# Revit family: DBLTD_TheSenatorGroup_LoungeChairs_Aura_Straight_US
name_source: partatom
category: Furniture
units: mm (PartAtom-declared; Revit-internal decimal feet)

## family parameters
Always vertical = Yes
Cut with Voids When Loaded = No
OmniClass Number = 23.40.20.00
OmniClass Title = General Furniture and Specialties
Render Appearance Source = Family Geometry
Room Calculation Point = No
Shared = Yes
Work Plane-Based = No

## types (26) — shared parameters
Assembly Code = E2020200
AssetType = Movable
Category = Pr_40_50_12_57 Office chairs
Color = Upholstery: Various Options Available
DurationUnit = years
ExpectedLife = 5
Finish = Upholstery: Various Options Available
Keynote = Pr_40_50_12_57 Office chairs
Manufacturer = The Senator Group
ManufacturerName = The Senator Group
ManufacturerURL = https://www.allermuir.com
Material = Cut Foam Seat Carcass | Fully Upholstered | Plastic Glides with Felt
Name = Lounge Sofa
NominalDepth = 38 "
ProductInformation = https://www.allermuir.com
SeatingHeight = 16 "
Shape = Rectangular
URL = https://www.thesenatorgroup.com
Uniclass2015Code = Pr_40_50_12_48
Uniclass2015Title = Lounge chairs
Uniclass2015Version = Products v1.39
Version = 1
WarrantyDescription = The Senator Group warrants that its manufactured products are free from manufacturing defects - in materials or workmanship - for a period of five (5) years.
WarrantyDurationLabor = 5
WarrantyDurationParts = 5
WarrantyDurationUnit = years
WarrantyGuarantorLabor = https://www.thesenatorgroup.com
WarrantyGuarantorParts = https://www.thesenatorgroup.com
zero-valued in all types: Cost, Default Elevation

## per-type parameters (varying)
| type | Constituents | HasLeftLink | HasRightLink | IsArray | IsSingle | Model | ModelNumber | NominalHeight | NominalWidth | Size | UnitArray | WithBack | WithoutBack |
| 1 Unit with Back and Left Link | Seat and Back | Yes | No | No | Yes | AURLS11L | AURLS11L | 30 " | 13 " | 29.5"h x 13"w x 38"d | 2 | Yes | No |
| 1 Unit with Back and Right Link | Seat and Back | No | Yes | No | Yes | AURLS11R | AURLS11R | 30 " | 13 " | 29.5"h x 13"w x 38"d | 2 | Yes | No |
| 1 Unit with Back and Both Links | Seat and Back | Yes | Yes | No | Yes | AURLS11M | AURLS11M | 30 " | 13 " | 29.5"h x 13"w x 38"d | 2 | Yes | No |
| 2 Units with Back and Left Link | Seat and Back | Yes | No | Yes | No | AURLS12L | AURLS12L | 30 " | 26 " | 29.5"h x 26"w x 38"d | 2 | Yes | No |
| 2 Units with Back and Right Link | Seat and Back | No | Yes | Yes | No | AURLS12R | AURLS12R | 30 " | 26 " | 29.5"h x 26"w x 38"d | 2 | Yes | No |
| 2 Units with Back and Both Links | Seat and Back | Yes | Yes | Yes | No | AURLS12M | AURLS12M | 30 " | 26 " | 29.5"h x 26"w x 38"d | 2 | Yes | No |
| 3 Units with Back and Left Link | Seat and Back | Yes | No | Yes | No | AURLS13L | AURLS13L | 30 " | 39 " | 29.5"h x 39"w x 38"d | 3 | Yes | No |
| 3 Units with Back and Right Link | Seat and Back | No | Yes | Yes | No | AURLS13R | AURLS13R | 30 " | 39 " | 29.5"h x 39"w x 38"d | 3 | Yes | No |
| 3 Units with Back and Both Links | Seat and Back | Yes | Yes | Yes | No | AURLS13M | AURLS13M | 30 " | 39 " | 29.5"h x 39"w x 38"d | 3 | Yes | No |
| 4 Units with Back and Left Link | Seat and Back | Yes | No | Yes | No | AURLS14L | AURLS14L | 30 " | 52 " | 29.5"h x 52"w x 38"d | 4 | Yes | No |
| 4 Units with Back and Right Link | Seat and Back | No | Yes | Yes | No | AURLS14R | AURLS14R | 30 " | 52 " | 29.5"h x 52"w x 38"d | 4 | Yes | No |
| 4 Units with Back and Both Links | Seat and Back | Yes | Yes | Yes | No | AURLS14M | AURLS14M | 30 " | 52 " | 29.5"h x 52"w x 38"d | 4 | Yes | No |
| 1 Unit with Left Link | Seat | Yes | No | No | Yes | AURLS01L | AURLS01L | 16 " | 13 " | 16.25"h x 13"w x 38"d | 2 | No | Yes |
| 1 Unit with Right Link | Seat | No | Yes | No | Yes | AURLS01R | AURLS01R | 16 " | 13 " | 16.25"h x 13"w x 38"d | 2 | No | Yes |
| 1 Unit with Both Links | Seat | Yes | Yes | No | Yes | AURLS01M | AURLS01M | 16 " | 13 " | 16.25"h x 13"w x 38"d | 2 | No | Yes |
| 2 Units with Left Link | Seat | Yes | No | Yes | No | AURLS02L | AURLS02L | 16 " | 26 " | 16.25"h x 26"w x 38"d | 2 | No | Yes |
| 2 Units with Right Link | Seat | No | Yes | Yes | No | AURLS02R | AURLS02R | 16 " | 26 " | 16.25"h x 26"w x 38"d | 2 | No | Yes |
| 2 Units with Both Links | Seat | Yes | Yes | Yes | No | AURLS02M | AURLS02M | 16 " | 26 " | 16.25"h x 26"w x 38"d | 2 | No | Yes |
| 3 Units with Left Link | Seat | Yes | No | Yes | No | AURLS03L | AURLS03L | 16 " | 39 " | 16.25"h x 39"w x 38"d | 3 | No | Yes |
| 3 Units with Right Link | Seat | No | Yes | Yes | No | AURLS03R | AURLS03R | 16 " | 39 " | 16.25"h x 39"w x 38"d | 3 | No | Yes |
| 3 Units with Both Links | Seat | Yes | Yes | Yes | No | AURLS03M | AURLS03M | 16 " | 39 " | 16.25"h x 39"w x 38"d | 3 | No | Yes |
| 4 Units with Left Link | Seat | Yes | No | Yes | No | AURLS04L | AURLS04L | 16 " | 52 " | 16.25"h x 52"w x 38"d | 4 | No | Yes |
| 4 Units with Right Link | Seat | No | Yes | Yes | No | AURLS04R | AURLS04R | 16 " | 52 " | 16.25"h x 52"w x 38"d | 4 | No | Yes |
| 4 Units with Both Links | Seat | Yes | Yes | Yes | No | AURLS04M | AURLS04M | 16 " | 52 " | 16.25"h x 52"w x 38"d | 4 | No | Yes |
| 4 Units with Back Standalone | Seat and Back | No | No | Yes | No | AURLS14 | AURLS14 | 30 " | 52 " | 29.5"h x 52"w x 38"d | 4 | Yes | No |
| 4 Units Standalone | Seat | No | No | Yes | No | AURLS04 | AURLS04 | 16 " | 52 " | 16.25"h x 52"w x 38"d | 4 | No | Yes |

note: column(s) folded — value = type name in every type: Description, ModelReference, Type Comments

## geometry (parser evidence)
native form markers: Sweep x6
no freeform markers — native parametric forms only
